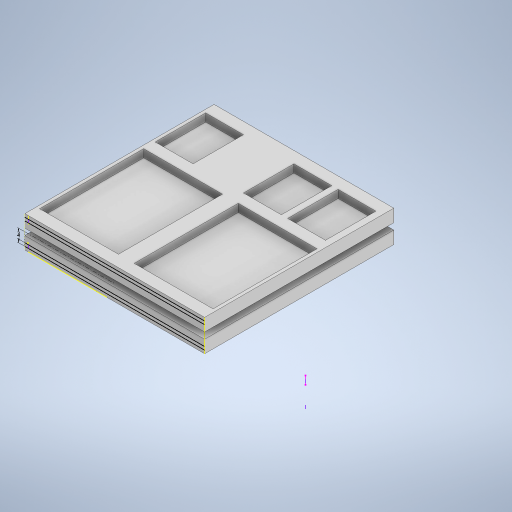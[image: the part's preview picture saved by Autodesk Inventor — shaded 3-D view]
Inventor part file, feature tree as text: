
AUTODESK INVENTOR PART (.ipt)
format: ipt  version: 2023 (Build 270158000, 158)  size: 381,952 bytes
history: native  units: mm
features: extrude x6, sketch x3
ambient origin geometry x8: Origin, YZ Plane, XZ Plane, XY Plane, X Axis, Y Axis, Z Axis, Center Point
bodies: Solido1 (feature_tree)
feature tree (9):
  sketch  "Schizzo1"
  extrude  "Estrusione1"  Depth=25.0mm
  extrude  "Estrusione2"  Depth=33.0mm
  extrude  "Estrusione5"  Depth=12.0mm
  extrude  "Estrusione6"  Depth=60.0mm
  extrude  "Estrusione7"  Depth=10.0mm TaperAngle=0.0deg
  extrude  "Estrusione8"  Depth=5.0mm TaperAngle=0.0deg
  sketch  "Schizzo3"
  sketch  "Schizzo4"
